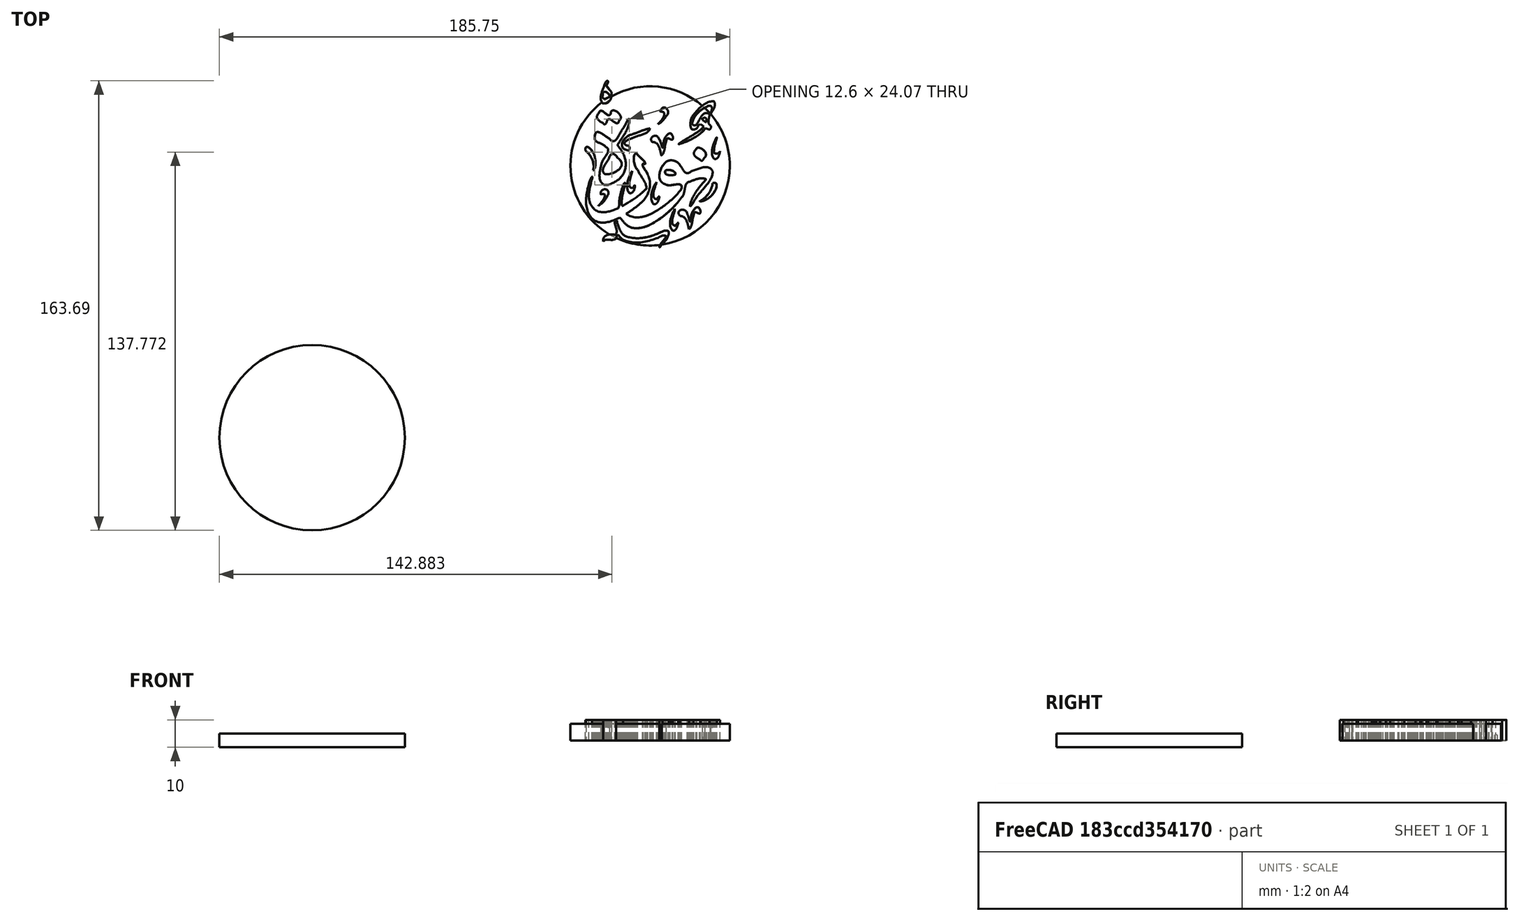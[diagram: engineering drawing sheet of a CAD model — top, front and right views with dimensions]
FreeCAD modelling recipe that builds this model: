
FCSTD DOCUMENT  (FreeCAD 0.20R29410 (Git))
Label: nora1
License: All rights reserved
LicenseURL: http://en.wikipedia.org/wiki/All_rights_reserved
objects: Part::Feature×24, Sketcher::SketchObject×4, Part::Extrusion×4, Part::FeaturePython×3, App::Part×1, Mesh::Feature×1, Part::Refine×1, Part::Cut×1
note: 37 computed .brp shape members not serialized (recipe doc carries the construction recipe); baked Part::Feature solids carry a one-line shape summary decoded from their .brp

FEATURE [Part::Feature] path177
  shape: bbox 57.29 x 21.69 x 2e-07 mm, 1 faces, 0 solids (baked)
FEATURE [Part::Feature] path177001
  shape: bbox 9.708 x 18.3 x 2e-07 mm, 1 faces, 0 solids (baked)
FEATURE [Part::Feature] path177002
  shape: bbox 21.06 x 22.96 x 2e-07 mm, 1 faces, 0 solids (baked)
FEATURE [Part::Feature] path177003
  shape: bbox 104.3 x 61.12 x 2e-07 mm, 1 faces, 0 solids (baked)
FEATURE [Part::Feature] path177004
  shape: bbox 13.98 x 7.897 x 2e-07 mm, 1 faces, 0 solids (baked)
FEATURE [Part::Feature] path177005
  shape: bbox 11.09 x 15.73 x 2e-07 mm, 1 faces, 0 solids (baked)
FEATURE [Part::Feature] path177006
  shape: bbox 10.01 x 18.37 x 2e-07 mm, 1 faces, 0 solids (baked)
FEATURE [Part::Feature] path177007
  shape: bbox 18.02 x 16.7 x 2e-07 mm, 1 faces, 0 solids (baked)
FEATURE [Part::Feature] path177008
  shape: bbox 10.13 x 17.99 x 2e-07 mm, 1 faces, 0 solids (baked)
FEATURE [Part::Feature] path177009
  shape: bbox 30.01 x 58.42 x 2e-07 mm, 1 faces, 0 solids (baked)
FEATURE [Part::Feature] path177010
  shape: bbox 22.46 x 18.13 x 2e-07 mm, 1 faces, 0 solids (baked)
FEATURE [Part::Feature] path177011
  shape: bbox 8.992 x 23.87 x 2e-07 mm, 1 faces, 0 solids (baked)
FEATURE [Part::Feature] path177012
  shape: bbox 15.79 x 14.72 x 2e-07 mm, 1 faces, 0 solids (baked)
FEATURE [Part::Feature] path177013
  shape: bbox 8.522 x 22.64 x 2e-07 mm, 1 faces, 0 solids (baked)
FEATURE [Part::Feature] path177014
  shape: bbox 20.93 x 22.58 x 2e-07 mm, 1 faces, 0 solids (baked)
FEATURE [Part::Feature] path177015
  shape: bbox 27.13 x 19.1 x 2e-07 mm, 1 faces, 0 solids (baked)
FEATURE [Part::Feature] path177016
  shape: bbox 31.46 x 34.86 x 2e-07 mm, 1 faces, 0 solids (baked)
FEATURE [Part::Feature] path177017
  shape: bbox 17.34 x 18.75 x 2e-07 mm, 1 faces, 0 solids (baked)
FEATURE [Part::Feature] path177018
  shape: bbox 8.777 x 5.87 x 2e-07 mm, 1 faces, 0 solids (baked)
FEATURE [Part::Feature] path177019
  shape: bbox 25.03 x 20.38 x 2e-07 mm, 1 faces, 0 solids (baked)
FEATURE [Part::Feature] path177020
  shape: bbox 11.54 x 17.72 x 2e-07 mm, 1 faces, 0 solids (baked)
FEATURE [Part::Feature] path177021
  shape: bbox 11.72 x 20.67 x 2e-07 mm, 1 faces, 0 solids (baked)
FEATURE [Part::Feature] path177022
  shape: bbox 10.73 x 10.48 x 2e-07 mm, 1 faces, 0 solids (baked)
FEATURE [Sketcher::SketchObject] Sketch
  FullyConstrained = false
  sketch-geometry (132):
    g0: BSplineCurve PolesCount=4 KnotsCount=2 Degree=3 IsPeriodic=0
    g1: BSplineCurve PolesCount=4 KnotsCount=2 Degree=3 IsPeriodic=0
    g2: BSplineCurve PolesCount=4 KnotsCount=2 Degree=3 IsPeriodic=0
    g3: BSplineCurve PolesCount=4 KnotsCount=2 Degree=3 IsPeriodic=0
    g4: BSplineCurve PolesCount=4 KnotsCount=2 Degree=3 IsPeriodic=0
    g5: BSplineCurve PolesCount=4 KnotsCount=2 Degree=3 IsPeriodic=0
    g6: BSplineCurve PolesCount=4 KnotsCount=2 Degree=3 IsPeriodic=0
    g7: BSplineCurve PolesCount=4 KnotsCount=2 Degree=3 IsPeriodic=0
    g8: BSplineCurve PolesCount=4 KnotsCount=2 Degree=3 IsPeriodic=0
    g9: BSplineCurve PolesCount=4 KnotsCount=2 Degree=3 IsPeriodic=0
    g10: BSplineCurve PolesCount=4 KnotsCount=2 Degree=3 IsPeriodic=0
    g11: BSplineCurve PolesCount=4 KnotsCount=2 Degree=3 IsPeriodic=0
    g12: BSplineCurve PolesCount=4 KnotsCount=2 Degree=3 IsPeriodic=0
    g13: BSplineCurve PolesCount=4 KnotsCount=2 Degree=3 IsPeriodic=0
    g14: BSplineCurve PolesCount=4 KnotsCount=2 Degree=3 IsPeriodic=0
    g15: BSplineCurve PolesCount=4 KnotsCount=2 Degree=3 IsPeriodic=0
    g16: BSplineCurve PolesCount=4 KnotsCount=2 Degree=3 IsPeriodic=0
    g17: BSplineCurve PolesCount=4 KnotsCount=2 Degree=3 IsPeriodic=0
    g18: BSplineCurve PolesCount=4 KnotsCount=2 Degree=3 IsPeriodic=0
    g19: BSplineCurve PolesCount=4 KnotsCount=2 Degree=3 IsPeriodic=0
    g20: BSplineCurve PolesCount=4 KnotsCount=2 Degree=3 IsPeriodic=0
    g21: BSplineCurve PolesCount=4 KnotsCount=2 Degree=3 IsPeriodic=0
    g22: BSplineCurve PolesCount=4 KnotsCount=2 Degree=3 IsPeriodic=0
    g23: BSplineCurve PolesCount=4 KnotsCount=2 Degree=3 IsPeriodic=0
    g24: BSplineCurve PolesCount=4 KnotsCount=2 Degree=3 IsPeriodic=0
    g25: BSplineCurve PolesCount=4 KnotsCount=2 Degree=3 IsPeriodic=0
    g26: BSplineCurve PolesCount=4 KnotsCount=2 Degree=3 IsPeriodic=0
    g27: BSplineCurve PolesCount=4 KnotsCount=2 Degree=3 IsPeriodic=0
    g28: BSplineCurve PolesCount=4 KnotsCount=2 Degree=3 IsPeriodic=0
    g29: BSplineCurve PolesCount=4 KnotsCount=2 Degree=3 IsPeriodic=0
    g30: BSplineCurve PolesCount=4 KnotsCount=2 Degree=3 IsPeriodic=0
    g31: BSplineCurve PolesCount=4 KnotsCount=2 Degree=3 IsPeriodic=0
    g32: BSplineCurve PolesCount=4 KnotsCount=2 Degree=3 IsPeriodic=0
    g33: BSplineCurve PolesCount=4 KnotsCount=2 Degree=3 IsPeriodic=0
    g34: BSplineCurve PolesCount=4 KnotsCount=2 Degree=3 IsPeriodic=0
    g35: BSplineCurve PolesCount=4 KnotsCount=2 Degree=3 IsPeriodic=0
    g36: BSplineCurve PolesCount=4 KnotsCount=2 Degree=3 IsPeriodic=0
    g37: BSplineCurve PolesCount=4 KnotsCount=2 Degree=3 IsPeriodic=0
    g38: BSplineCurve PolesCount=4 KnotsCount=2 Degree=3 IsPeriodic=0
    g39: BSplineCurve PolesCount=4 KnotsCount=2 Degree=3 IsPeriodic=0
    g40: BSplineCurve PolesCount=4 KnotsCount=2 Degree=3 IsPeriodic=0
    g41: BSplineCurve PolesCount=4 KnotsCount=2 Degree=3 IsPeriodic=0
    g42: BSplineCurve PolesCount=4 KnotsCount=2 Degree=3 IsPeriodic=0
    g43: BSplineCurve PolesCount=4 KnotsCount=2 Degree=3 IsPeriodic=0
    g44: BSplineCurve PolesCount=4 KnotsCount=2 Degree=3 IsPeriodic=0
    g45: BSplineCurve PolesCount=4 KnotsCount=2 Degree=3 IsPeriodic=0
    g46: BSplineCurve PolesCount=4 KnotsCount=2 Degree=3 IsPeriodic=0
    g47: BSplineCurve PolesCount=4 KnotsCount=2 Degree=3 IsPeriodic=0
    g48: BSplineCurve PolesCount=4 KnotsCount=2 Degree=3 IsPeriodic=0
    g49: BSplineCurve PolesCount=4 KnotsCount=2 Degree=3 IsPeriodic=0
    g50: BSplineCurve PolesCount=4 KnotsCount=2 Degree=3 IsPeriodic=0
    g51: BSplineCurve PolesCount=4 KnotsCount=2 Degree=3 IsPeriodic=0
    g52: BSplineCurve PolesCount=4 KnotsCount=2 Degree=3 IsPeriodic=0
    g53: BSplineCurve PolesCount=4 KnotsCount=2 Degree=3 IsPeriodic=0
    g54: BSplineCurve PolesCount=4 KnotsCount=2 Degree=3 IsPeriodic=0
    g55: BSplineCurve PolesCount=4 KnotsCount=2 Degree=3 IsPeriodic=0
    g56: BSplineCurve PolesCount=4 KnotsCount=2 Degree=3 IsPeriodic=0
    g57: BSplineCurve PolesCount=4 KnotsCount=2 Degree=3 IsPeriodic=0
    g58: BSplineCurve PolesCount=4 KnotsCount=2 Degree=3 IsPeriodic=0
    g59: BSplineCurve PolesCount=4 KnotsCount=2 Degree=3 IsPeriodic=0
    g60: BSplineCurve PolesCount=4 KnotsCount=2 Degree=3 IsPeriodic=0
    g61: BSplineCurve PolesCount=4 KnotsCount=2 Degree=3 IsPeriodic=0
    g62: BSplineCurve PolesCount=4 KnotsCount=2 Degree=3 IsPeriodic=0
    g63: BSplineCurve PolesCount=4 KnotsCount=2 Degree=3 IsPeriodic=0
    g64: BSplineCurve PolesCount=4 KnotsCount=2 Degree=3 IsPeriodic=0
    g65: BSplineCurve PolesCount=2 KnotsCount=2 Degree=1 IsPeriodic=0
    g66: BSplineCurve PolesCount=2 KnotsCount=2 Degree=1 IsPeriodic=0
    g67: BSplineCurve PolesCount=4 KnotsCount=2 Degree=3 IsPeriodic=0
    g68: BSplineCurve PolesCount=4 KnotsCount=2 Degree=3 IsPeriodic=0
    g69: BSplineCurve PolesCount=4 KnotsCount=2 Degree=3 IsPeriodic=0
    g70: BSplineCurve PolesCount=4 KnotsCount=2 Degree=3 IsPeriodic=0
    g71: BSplineCurve PolesCount=4 KnotsCount=2 Degree=3 IsPeriodic=0
    g72: BSplineCurve PolesCount=4 KnotsCount=2 Degree=3 IsPeriodic=0
    g73: BSplineCurve PolesCount=4 KnotsCount=2 Degree=3 IsPeriodic=0
    g74: BSplineCurve PolesCount=4 KnotsCount=2 Degree=3 IsPeriodic=0
    g75: BSplineCurve PolesCount=4 KnotsCount=2 Degree=3 IsPeriodic=0
    g76: BSplineCurve PolesCount=4 KnotsCount=2 Degree=3 IsPeriodic=0
    g77: BSplineCurve PolesCount=4 KnotsCount=2 Degree=3 IsPeriodic=0
    g78: BSplineCurve PolesCount=4 KnotsCount=2 Degree=3 IsPeriodic=0
    g79: BSplineCurve PolesCount=4 KnotsCount=2 Degree=3 IsPeriodic=0
    g80: BSplineCurve PolesCount=4 KnotsCount=2 Degree=3 IsPeriodic=0
    g81: BSplineCurve PolesCount=4 KnotsCount=2 Degree=3 IsPeriodic=0
    g82: BSplineCurve PolesCount=4 KnotsCount=2 Degree=3 IsPeriodic=0
    g83: BSplineCurve PolesCount=4 KnotsCount=2 Degree=3 IsPeriodic=0
    g84: BSplineCurve PolesCount=4 KnotsCount=2 Degree=3 IsPeriodic=0
    g85: BSplineCurve PolesCount=4 KnotsCount=2 Degree=3 IsPeriodic=0
    g86: BSplineCurve PolesCount=4 KnotsCount=2 Degree=3 IsPeriodic=0
    g87: BSplineCurve PolesCount=4 KnotsCount=2 Degree=3 IsPeriodic=0
    g88: BSplineCurve PolesCount=4 KnotsCount=2 Degree=3 IsPeriodic=0
    g89: BSplineCurve PolesCount=4 KnotsCount=2 Degree=3 IsPeriodic=0
    g90: BSplineCurve PolesCount=4 KnotsCount=2 Degree=3 IsPeriodic=0
    g91: BSplineCurve PolesCount=4 KnotsCount=2 Degree=3 IsPeriodic=0
    g92: BSplineCurve PolesCount=4 KnotsCount=2 Degree=3 IsPeriodic=0
    g93: BSplineCurve PolesCount=4 KnotsCount=2 Degree=3 IsPeriodic=0
    g94: BSplineCurve PolesCount=4 KnotsCount=2 Degree=3 IsPeriodic=0
    g95: BSplineCurve PolesCount=4 KnotsCount=2 Degree=3 IsPeriodic=0
    g96: BSplineCurve PolesCount=4 KnotsCount=2 Degree=3 IsPeriodic=0
    g97: BSplineCurve PolesCount=4 KnotsCount=2 Degree=3 IsPeriodic=0
    g98: BSplineCurve PolesCount=4 KnotsCount=2 Degree=3 IsPeriodic=0
    g99: BSplineCurve PolesCount=4 KnotsCount=2 Degree=3 IsPeriodic=0
    g100: BSplineCurve PolesCount=4 KnotsCount=2 Degree=3 IsPeriodic=0
    g101: BSplineCurve PolesCount=4 KnotsCount=2 Degree=3 IsPeriodic=0
    g102: BSplineCurve PolesCount=4 KnotsCount=2 Degree=3 IsPeriodic=0
    g103: BSplineCurve PolesCount=4 KnotsCount=2 Degree=3 IsPeriodic=0
    g104: BSplineCurve PolesCount=4 KnotsCount=2 Degree=3 IsPeriodic=0
    g105: BSplineCurve PolesCount=4 KnotsCount=2 Degree=3 IsPeriodic=0
    g106: BSplineCurve PolesCount=4 KnotsCount=2 Degree=3 IsPeriodic=0
    g107: BSplineCurve PolesCount=4 KnotsCount=2 Degree=3 IsPeriodic=0
    g108: BSplineCurve PolesCount=4 KnotsCount=2 Degree=3 IsPeriodic=0
    g109: BSplineCurve PolesCount=4 KnotsCount=2 Degree=3 IsPeriodic=0
    g110: BSplineCurve PolesCount=2 KnotsCount=2 Degree=1 IsPeriodic=0
    g111: BSplineCurve PolesCount=4 KnotsCount=2 Degree=3 IsPeriodic=0
    g112: BSplineCurve PolesCount=4 KnotsCount=2 Degree=3 IsPeriodic=0
    g113: BSplineCurve PolesCount=4 KnotsCount=2 Degree=3 IsPeriodic=0
    g114: BSplineCurve PolesCount=4 KnotsCount=2 Degree=3 IsPeriodic=0
    g115: BSplineCurve PolesCount=4 KnotsCount=2 Degree=3 IsPeriodic=0
    g116: BSplineCurve PolesCount=2 KnotsCount=2 Degree=1 IsPeriodic=0
    g117: BSplineCurve PolesCount=2 KnotsCount=2 Degree=1 IsPeriodic=0
    g118: BSplineCurve PolesCount=4 KnotsCount=2 Degree=3 IsPeriodic=0
    g119: BSplineCurve PolesCount=4 KnotsCount=2 Degree=3 IsPeriodic=0
    g120: BSplineCurve PolesCount=4 KnotsCount=2 Degree=3 IsPeriodic=0
    g121: BSplineCurve PolesCount=4 KnotsCount=2 Degree=3 IsPeriodic=0
    g122: BSplineCurve PolesCount=4 KnotsCount=2 Degree=3 IsPeriodic=0
    g123: BSplineCurve PolesCount=4 KnotsCount=2 Degree=3 IsPeriodic=0
    g124: BSplineCurve PolesCount=4 KnotsCount=2 Degree=3 IsPeriodic=0
    g125: BSplineCurve PolesCount=4 KnotsCount=2 Degree=3 IsPeriodic=0
    g126: BSplineCurve PolesCount=4 KnotsCount=2 Degree=3 IsPeriodic=0
    g127: BSplineCurve PolesCount=4 KnotsCount=2 Degree=3 IsPeriodic=0
    g128: BSplineCurve PolesCount=4 KnotsCount=2 Degree=3 IsPeriodic=0
    g129: BSplineCurve PolesCount=4 KnotsCount=2 Degree=3 IsPeriodic=0
    g130: BSplineCurve PolesCount=4 KnotsCount=2 Degree=3 IsPeriodic=0
    g131: BSplineCurve PolesCount=4 KnotsCount=2 Degree=3 IsPeriodic=0
  constraints (132):
    c: Coincident(g0,g1)
    c: Coincident(g1,g2)
    c: Coincident(g2,g3)
    c: Coincident(g3,g4)
    c: Coincident(g4,g5)
    c: Coincident(g5,g6)
    c: Coincident(g6,g7)
    c: Coincident(g7,g8)
    c: Coincident(g8,g9)
    c: Coincident(g9,g0)
    c: Coincident(g10,g11)
    c: Coincident(g11,g12)
    c: Coincident(g12,g13)
    c: Coincident(g13,g10)
    c: Coincident(g14,g15)
    c: Coincident(g15,g16)
    c: Coincident(g16,g17)
    c: Coincident(g17,g18)
    c: Coincident(g18,g19)
    c: Coincident(g19,g14)
    c: Coincident(g20,g21)
    c: Coincident(g21,g22)
    c: Coincident(g22,g23)
    c: Coincident(g23,g24)
    c: Coincident(g24,g25)
    c: Coincident(g25,g26)
    c: Coincident(g26,g27)
    c: Coincident(g27,g28)
    c: Coincident(g28,g29)
    c: Coincident(g29,g30)
    c: Coincident(g30,g31)
    c: Coincident(g31,g32)
    c: Coincident(g32,g33)
    c: Coincident(g33,g34)
    c: Coincident(g34,g35)
    c: Coincident(g35,g36)
    c: Coincident(g36,g37)
    c: Coincident(g37,g38)
    c: Coincident(g38,g39)
    c: Coincident(g39,g40)
    c: Coincident(g40,g41)
    c: Coincident(g41,g42)
    c: Coincident(g42,g43)
    c: Coincident(g43,g44)
    c: Coincident(g44,g45)
    c: Coincident(g45,g46)
    c: Coincident(g46,g47)
    c: Coincident(g47,g48)
    c: Coincident(g48,g49)
    c: Coincident(g49,g20)
    c: Coincident(g50,g51)
    c: Coincident(g51,g50)
    c: Coincident(g52,g53)
    c: Coincident(g53,g54)
    c: Coincident(g54,g52)
    c: Coincident(g55,g56)
    c: Coincident(g56,g57)
    c: Coincident(g57,g58)
    c: Coincident(g58,g55)
    c: Coincident(g59,g60)
    c: Coincident(g60,g61)
    c: Coincident(g61,g59)
    c: Coincident(g62,g63)
    c: Coincident(g63,g64)
    c: Coincident(g64,g65)
    c: Coincident(g65,g66)
    c: Coincident(g66,g62)
    c: Coincident(g67,g68)
    c: Coincident(g68,g69)
    c: Coincident(g69,g70)
    c: Coincident(g70,g71)
    c: Coincident(g71,g72)
    c: Coincident(g72,g73)
    c: Coincident(g73,g74)
    c: Coincident(g74,g75)
    c: Coincident(g75,g76)
    c: Coincident(g76,g67)
    c: Coincident(g77,g78)
    c: Coincident(g78,g79)
    c: Coincident(g79,g80)
    c: Coincident(g80,g77)
    c: Coincident(g81,g82)
    c: Coincident(g82,g83)
    c: Coincident(g83,g81)
    c: Coincident(g84,g85)
    c: Coincident(g85,g86)
    c: Coincident(g86,g84)
    c: Coincident(g87,g88)
    c: Coincident(g88,g89)
    c: Coincident(g89,g90)
    c: Coincident(g90,g87)
    c: Coincident(g91,g92)
    c: Coincident(g92,g93)
    c: Coincident(g93,g94)
    c: Coincident(g94,g95)
    c: Coincident(g95,g96)
    c: Coincident(g96,g91)
    c: Coincident(g97,g98)
    c: Coincident(g98,g99)
    c: Coincident(g99,g100)
    c: Coincident(g100,g101)
    c: Coincident(g101,g97)
    c: Coincident(g102,g103)
    c: Coincident(g103,g104)
    c: Coincident(g104,g105)
    c: Coincident(g105,g106)
    c: Coincident(g106,g107)
    c: Coincident(g107,g108)
    c: Coincident(g108,g109)
    c: Coincident(g109,g110)
    c: Coincident(g110,g102)
    c: Coincident(g111,g112)
    c: Coincident(g112,g113)
    c: Coincident(g113,g114)
    c: Coincident(g114,g111)
    c: Coincident(g115,g116)
    c: Coincident(g116,g117)
    c: Coincident(g117,g115)
    c: Coincident(g118,g119)
    c: Coincident(g119,g120)
    c: Coincident(g120,g121)
    c: Coincident(g121,g122)
    c: Coincident(g122,g118)
    c: Coincident(g123,g124)
    c: Coincident(g124,g125)
    c: Coincident(g125,g123)
    c: Coincident(g126,g127)
    c: Coincident(g127,g128)
    c: Coincident(g128,g129)
    c: Coincident(g129,g126)
    c: Coincident(g130,g131)
    c: Coincident(g131,g130)
FEATURE [Part::Extrusion] Extrude
  Base = -> Sketch
  Dir = (0,0,1)
  DirMode = 2
  FaceMakerClass = Part::FaceMakerBullseye
  LengthFwd = 10
  LengthRev = 0
  Placement = pos=(-109,145,0) rot=(0,0,1;0rad)
  Solid = true
  Symmetric = false
FEATURE [Sketcher::SketchObject] Sketch001
  FullyConstrained = false
  MapMode = 2
  Placement = pos=(-109,145,0) rot=(0,0,1;0rad)
  Support = -> [Extrude]
  sketch-geometry (1):
    g0: Circle CenterX=108.298 CenterY=-137.609 CenterZ=0 NormalX=0 NormalY=0 NormalZ=1 AngleXU=0 Radius=33.75
  constraints (1):
    c: Diameter(g0) = 67.5
FEATURE [Part::FeaturePython] Clone  label="Nora-scaled"  # Draft clone (typed FeaturePython)
  AttacherType = Attacher::AttachEngine3D
  Fuse = false
  Objects = -> [Extrude]
  Placement = pos=(73.85,168.01,0) rot=(0,0,1;0rad)
  Scale = (0.45,0.45,0.75)
FEATURE [Part::Extrusion] Extrude001  label="Extrude002"
  Base = -> Sketch001
  Dir = (0,0,1)
  DirMode = 2
  FaceMakerClass = Part::FaceMakerBullseye
  LengthFwd = 5
  LengthRev = 0
  Solid = true
  Symmetric = true
FEATURE [App::Part] Part
  Group = -> [Sketch001,Extrude001,Sketch,Extrude]
  Origin = -> Origin
FEATURE [Mesh::Feature] tangledsun_20140330_160mm
FEATURE [Part::Feature] tangledsun_20140330_160mm001
  shape: bbox 159.2 x 161.2 x 9.452 mm, 9688 faces, 0 solids (baked)
FEATURE [Part::Refine] tangledsun_20140330_160mm001001
  Source = -> tangledsun_20140330_160mm001
FEATURE [Sketcher::SketchObject] Sketch002
  FullyConstrained = false
  MapMode = 5
  Placement = pos=(0,0,0) rot=(1,0,0;3.14159rad)
  Support = -> [tangledsun_20140330_160mm001001]
  sketch-geometry (1):
    g0: Circle CenterX=122.485 CenterY=-106.3 CenterZ=0 NormalX=0 NormalY=0 NormalZ=1 AngleXU=0 Radius=28.29
  constraints (1):
    c: Radius(g0) = 28.29
FEATURE [Part::Extrusion] Extrude002  label="Extrude003"
  Base = -> Sketch002
  Dir = (0,0,-1)
  DirMode = 2
  FaceMakerClass = Part::FaceMakerBullseye
  LengthFwd = 20
  LengthRev = 0
  Placement = pos=(0,0,15) rot=(0,0,1;0rad)
  Solid = true
  Symmetric = false
FEATURE [Part::Cut] Cut  label="Pbase_sun"
  Base = -> tangledsun_20140330_160mm001001
  Refine = true
  Tool = -> Extrude002
FEATURE [Sketcher::SketchObject] Sketch003
  FullyConstrained = false
  MapMode = 5
  Placement = pos=(0,0,0) rot=(1,0,0;3.14159rad)
  Support = -> [Cut]
  sketch-geometry (1):
    g0: Circle CenterX=122.301 CenterY=-106.352 CenterZ=0 NormalX=0 NormalY=0 NormalZ=1 AngleXU=0 Radius=29
  constraints (1):
    c: Radius(g0) = 29
FEATURE [Part::Extrusion] Extrude003  label="Pcenter"
  Base = -> Sketch003
  Dir = (0,0,-1)
  DirMode = 2
  FaceMakerClass = Part::FaceMakerBullseye
  LengthFwd = 6
  LengthRev = 0
  Reversed = true
  Solid = true
  Symmetric = false
FEATURE [Part::FeaturePython] BooleanFragments  # WARN: FeaturePython — macro-defined, semantics opaque (R4)
  Mode = 0
  Objects = -> [Clone,Extrude003]
  Tolerance = 0
FEATURE [Part::FeaturePython] BooleanFragments001  label="NoraFinal"  # WARN: FeaturePython — macro-defined, semantics opaque (R4)
  Mode = 0
  Objects = -> [Cut,BooleanFragments]
  Tolerance = 0
